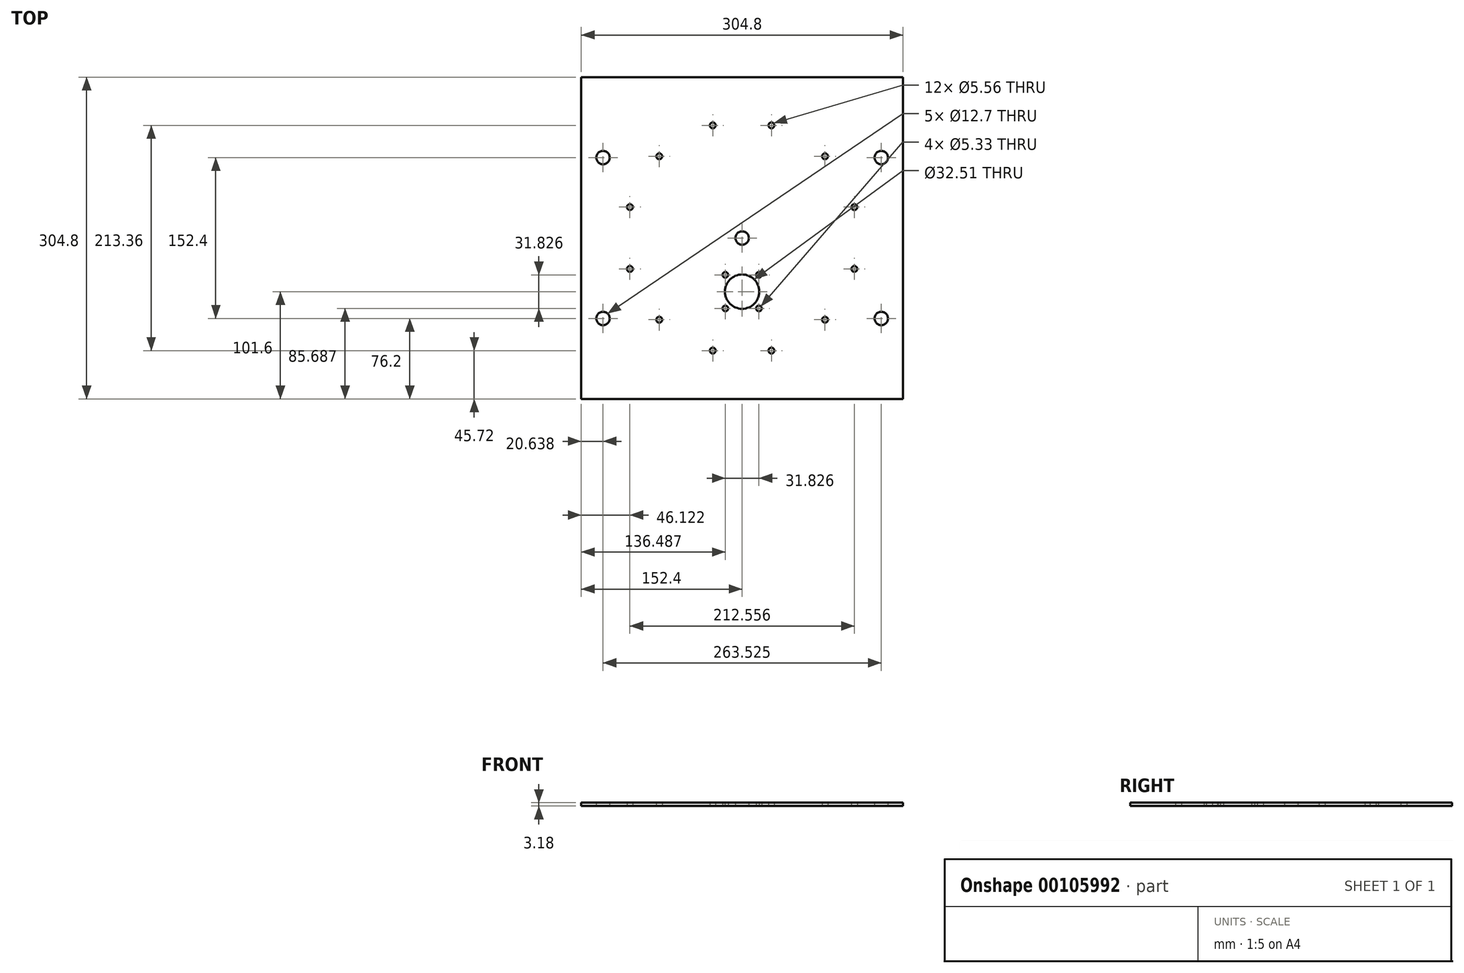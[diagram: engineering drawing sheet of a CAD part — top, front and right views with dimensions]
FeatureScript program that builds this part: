
annotation { "Feature Type Name" : "Feature", "Feature Type Description" : "" }
export const myFeature = defineFeature(function(context is Context, id is Id, definition is map)
    precondition{}
    {
        {
            var Q0;
            Q0=qCreatedBy(makeId("Top.planeOp"),FACE);
            var sketch = newSketch(context, id + "F0", { "sketchPlane" : qUnion([Q0])});
            skCircle(sketch, "E0", {"center": v(0, 0) * mm, "radius": 16.26 * mm});
            skCircle(sketch, "E1", {"center": v(0, 0) * mm, "radius": 22.5 * mm, "construction": true});
            skLineSegment(sketch, "E2", {"start": v(0, 0) * mm, "end": v(15.91, 15.91) * mm, "construction": true});
            skLineSegment(sketch, "E3", {"start": v(0, 0) * mm, "end": v(-15.91, -15.91) * mm, "construction": true});
            skLineSegment(sketch, "E4", {"start": v(0, 0) * mm, "end": v(-15.91, 15.91) * mm, "construction": true});
            skLineSegment(sketch, "E5", {"start": v(0, 0) * mm, "end": v(15.91, -15.91) * mm, "construction": true});
            skLineSegment(sketch, "E6", {"start": v(0, 0) * mm, "end": v(22.5, 0) * mm, "construction": true});
            skLineSegment(sketch, "E7", {"start": v(0, 0) * mm, "end": v(-22.5, 0) * mm, "construction": true});
            skLineSegment(sketch, "E8", {"start": v(0, 0) * mm, "end": v(0, 22.5) * mm, "construction": true});
            skLineSegment(sketch, "E9", {"start": v(0, 0) * mm, "end": v(0, -22.5) * mm, "construction": true});
            skCircle(sketch, "E10", {"center": v(-15.91, 15.91) * mm, "radius": 2.67 * mm});
            skCircle(sketch, "E11", {"center": v(15.91, 15.91) * mm, "radius": 2.67 * mm});
            skCircle(sketch, "E12", {"center": v(15.91, -15.91) * mm, "radius": 2.67 * mm});
            skCircle(sketch, "E13", {"center": v(-15.91, -15.91) * mm, "radius": 2.67 * mm});
            skLineSegment(sketch, "E14.bottom", {"start": v(-152.4, 203.2) * mm, "end": v(152.4, 203.2) * mm});
            skLineSegment(sketch, "E14.top", {"start": v(-152.4, -101.6) * mm, "end": v(152.4, -101.6) * mm});
            skLineSegment(sketch, "E14.left", {"start": v(-152.4, 203.2) * mm, "end": v(-152.4, -101.6) * mm});
            skLineSegment(sketch, "E14.right", {"start": v(152.4, 203.2) * mm, "end": v(152.4, -101.6) * mm});
            skPoint(sketch, "E15", {"position": v(0, 50.8) * mm});
            skCircle(sketch, "E16", {"center": v(0, 50.8) * mm, "radius": 106.68 * mm, "construction": true});
            skLineSegment(sketch, "E17", {"start": v(0, 50.8) * mm, "end": v(-106.68, 50.8) * mm, "construction": true});
            skLineSegment(sketch, "E18", {"start": v(0, 50.8) * mm, "end": v(106.68, 50.8) * mm, "construction": true});
            skLineSegment(sketch, "E19", {"start": v(0, 50.8) * mm, "end": v(0, 157.48) * mm, "construction": true});
            skLineSegment(sketch, "E20", {"start": v(0, 50.8) * mm, "end": v(-92.39, 104.14) * mm, "construction": true});
            skLineSegment(sketch, "E21", {"start": v(0, 50.8) * mm, "end": v(0, -55.88) * mm, "construction": true});
            skLineSegment(sketch, "E22", {"start": v(0, 50.8) * mm, "end": v(92.39, -2.54) * mm, "construction": true});
            skLineSegment(sketch, "E23", {"start": v(-92.39, 104.14) * mm, "end": v(-78.5, 128.2) * mm, "construction": true});
            skLineSegment(sketch, "E24", {"start": v(-92.39, 104.14) * mm, "end": v(-106.28, 80.08) * mm, "construction": true});
            skLineSegment(sketch, "E25", {"start": v(0, -55.88) * mm, "end": v(27.78, -55.88) * mm, "construction": true});
            skLineSegment(sketch, "E26", {"start": v(0, -55.88) * mm, "end": v(-27.78, -55.88) * mm, "construction": true});
            skLineSegment(sketch, "E27", {"start": v(92.39, -2.54) * mm, "end": v(78.5, -26.6) * mm, "construction": true});
            skLineSegment(sketch, "E28", {"start": v(92.39, -2.54) * mm, "end": v(106.28, 21.52) * mm, "construction": true});
            skLineSegment(sketch, "E29", {"start": v(0, 157.48) * mm, "end": v(27.78, 157.48) * mm, "construction": true});
            skLineSegment(sketch, "E30", {"start": v(0, 157.48) * mm, "end": v(-27.78, 157.48) * mm, "construction": true});
            skCircle(sketch, "E31", {"center": v(-78.5, 128.2) * mm, "radius": 2.78 * mm});
            skCircle(sketch, "E32", {"center": v(-106.28, 80.08) * mm, "radius": 2.78 * mm});
            skCircle(sketch, "E33", {"center": v(-27.78, -55.88) * mm, "radius": 2.78 * mm});
            skCircle(sketch, "E34", {"center": v(27.78, -55.88) * mm, "radius": 2.78 * mm});
            skCircle(sketch, "E35", {"center": v(78.5, -26.6) * mm, "radius": 2.78 * mm});
            skCircle(sketch, "E36", {"center": v(106.28, 21.52) * mm, "radius": 2.78 * mm});
            skCircle(sketch, "E37", {"center": v(27.78, 157.48) * mm, "radius": 2.78 * mm});
            skCircle(sketch, "E38", {"center": v(-27.78, 157.48) * mm, "radius": 2.78 * mm});
            skCircle(sketch, "E39", {"center": v(0, 50.8) * mm, "radius": 6.35 * mm});
            skLineSegment(sketch, "E40.bottom", {"start": v(-152.4, -101.6) * mm, "end": v(-131.76, -101.6) * mm, "construction": true});
            skLineSegment(sketch, "E40.top", {"start": v(-152.4, -25.4) * mm, "end": v(-131.76, -25.4) * mm, "construction": true});
            skLineSegment(sketch, "E40.left", {"start": v(-152.4, -101.6) * mm, "end": v(-152.4, -25.4) * mm, "construction": true});
            skLineSegment(sketch, "E40.right", {"start": v(-131.76, -101.6) * mm, "end": v(-131.76, -25.4) * mm, "construction": true});
            skLineSegment(sketch, "E41.bottom", {"start": v(-152.4, 203.2) * mm, "end": v(-131.76, 203.2) * mm, "construction": true});
            skLineSegment(sketch, "E41.top", {"start": v(-152.4, 127) * mm, "end": v(-131.76, 127) * mm, "construction": true});
            skLineSegment(sketch, "E41.left", {"start": v(-152.4, 203.2) * mm, "end": v(-152.4, 127) * mm, "construction": true});
            skLineSegment(sketch, "E41.right", {"start": v(-131.76, 203.2) * mm, "end": v(-131.76, 127) * mm, "construction": true});
            skLineSegment(sketch, "E42.bottom", {"start": v(152.4, 203.2) * mm, "end": v(131.76, 203.2) * mm, "construction": true});
            skLineSegment(sketch, "E42.top", {"start": v(152.4, 127) * mm, "end": v(131.76, 127) * mm, "construction": true});
            skLineSegment(sketch, "E42.left", {"start": v(152.4, 203.2) * mm, "end": v(152.4, 127) * mm, "construction": true});
            skLineSegment(sketch, "E42.right", {"start": v(131.76, 203.2) * mm, "end": v(131.76, 127) * mm, "construction": true});
            skLineSegment(sketch, "E43.bottom", {"start": v(152.4, -101.6) * mm, "end": v(131.76, -101.6) * mm, "construction": true});
            skLineSegment(sketch, "E43.top", {"start": v(152.4, -25.4) * mm, "end": v(131.76, -25.4) * mm, "construction": true});
            skLineSegment(sketch, "E43.left", {"start": v(152.4, -101.6) * mm, "end": v(152.4, -25.4) * mm, "construction": true});
            skLineSegment(sketch, "E43.right", {"start": v(131.76, -101.6) * mm, "end": v(131.76, -25.4) * mm, "construction": true});
            skCircle(sketch, "E44", {"center": v(-131.76, 127) * mm, "radius": 6.35 * mm});
            skCircle(sketch, "E45", {"center": v(131.76, 127) * mm, "radius": 6.35 * mm});
            skCircle(sketch, "E46", {"center": v(131.76, -25.4) * mm, "radius": 6.35 * mm});
            skCircle(sketch, "E47", {"center": v(-131.76, -25.4) * mm, "radius": 6.35 * mm});
            skLineSegment(sketch, "E48", {"start": v(0, 50.8) * mm, "end": v(92.39, 104.14) * mm, "construction": true});
            skLineSegment(sketch, "E49", {"start": v(92.39, 104.14) * mm, "end": v(78.5, 128.2) * mm, "construction": true});
            skLineSegment(sketch, "E50", {"start": v(92.39, 104.14) * mm, "end": v(106.28, 80.08) * mm, "construction": true});
            skCircle(sketch, "E51", {"center": v(106.28, 80.08) * mm, "radius": 2.78 * mm});
            skCircle(sketch, "E52", {"center": v(78.5, 128.2) * mm, "radius": 2.78 * mm});
            skLineSegment(sketch, "E53", {"start": v(0, 50.8) * mm, "end": v(-92.39, -2.54) * mm, "construction": true});
            skLineSegment(sketch, "E54", {"start": v(-92.39, -2.54) * mm, "end": v(-106.28, 21.52) * mm, "construction": true});
            skLineSegment(sketch, "E55", {"start": v(-92.39, -2.54) * mm, "end": v(-78.5, -26.6) * mm, "construction": true});
            skCircle(sketch, "E56", {"center": v(-106.28, 21.52) * mm, "radius": 2.78 * mm});
            skCircle(sketch, "E57", {"center": v(-78.5, -26.6) * mm, "radius": 2.78 * mm});
            skSolve(sketch);
        }
        {
            var Q0;
            Q0=makeQuery(id+"F0.imprint","IMPRINT",FACE,{"disambiguationData":[TD([[makeQuery(id+"F0.imprint","IMPRINT",EDGE,{"derivedFrom":sQuery(id+"F0.wireOp",EDGE,"E0")}),-1.0]])]});
            extrude(context, id + "F1", {"entities" : qUnion([Q0]), "depth" : 3.17 * mm});
        }
    });
